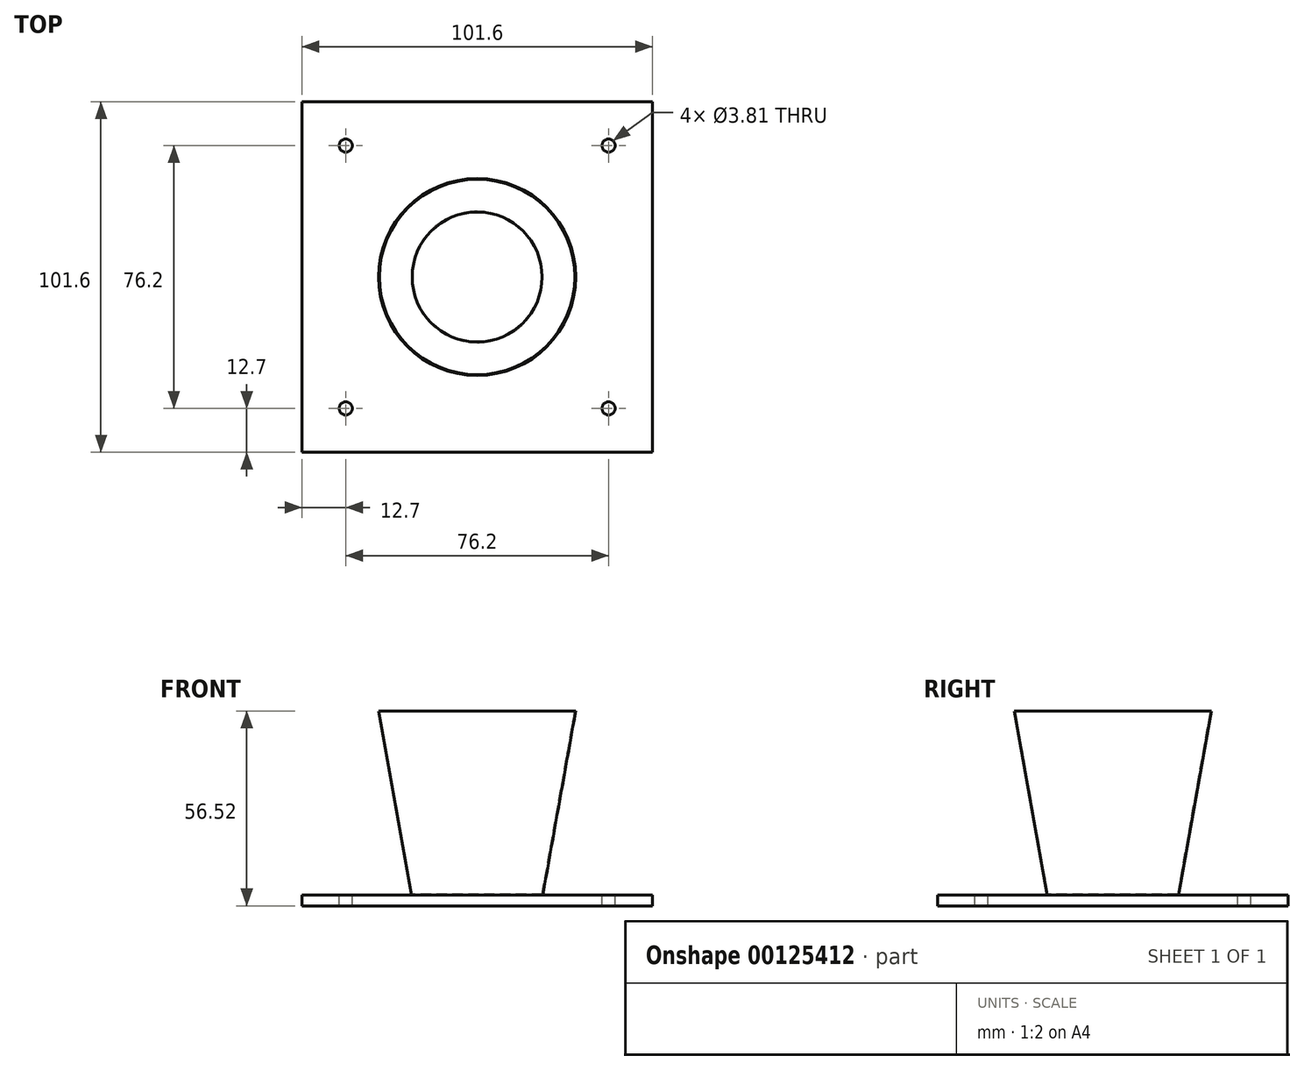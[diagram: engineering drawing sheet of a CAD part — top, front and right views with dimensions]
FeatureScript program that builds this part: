
annotation { "Feature Type Name" : "Feature", "Feature Type Description" : "" }
export const myFeature = defineFeature(function(context is Context, id is Id, definition is map)
    precondition{}
    {
        {
            var Q0;
            Q0=qCreatedBy(makeId("Top.planeOp"),FACE);
            var sketch = newSketch(context, id + "F0", { "sketchPlane" : qUnion([Q0])});
            skCircle(sketch, "E0", {"center": v(0, 0) * mm, "radius": 19.05 * mm});
            skSolve(sketch);
        }
        {
            var Q0;
            Q0=qCreatedBy(makeId("Top.planeOp"),FACE);
            cPlane(context, id + "F1", {"entities" : qUnion([Q0]), "cplaneType" : CPlaneType.OFFSET, "offset" : 53.34 * mm, "width" : 152.4 * mm, "height" : 152.4 * mm});
        }
        {
            var Q0;
            Q0=qCreatedBy(id+"F1.planeOp",FACE);
            var sketch = newSketch(context, id + "F2", { "sketchPlane" : qUnion([Q0])});
            skCircle(sketch, "E1", {"center": v(0, 0) * mm, "radius": 28.58 * mm});
            skSolve(sketch);
        }
        {
            var Q0;
            Q0=makeQuery(id+"F2.imprint","IMPRINT",FACE,{"disambiguationData":[TD([[makeQuery(id+"F2.imprint","IMPRINT",EDGE,{"derivedFrom":sQuery(id+"F2.wireOp",EDGE,"E1")}),1.0]])]});
            var Q1;
            Q1=makeQuery(id+"F0.imprint","IMPRINT",FACE,{"disambiguationData":[TD([[makeQuery(id+"F0.imprint","IMPRINT",EDGE,{"derivedFrom":sQuery(id+"F0.wireOp",EDGE,"E0")}),1.0]])]});
            loft(context, id + "F3", {"sheetProfilesArray" : [{ "sheetProfileEntities" : qUnion([Q0]) }, { "sheetProfileEntities" : qUnion([Q1]) }]});
        }
        {
            var Q0;
            Q0=makeQuery(id+"F3.opLoft","CAP_FACE",FACE,{"disambiguationData":[OSD([makeQuery(id+"F2.imprint","IMPRINT",FACE,{"disambiguationData":[TD([[makeQuery(id+"F2.imprint","IMPRINT",EDGE,{"derivedFrom":sQuery(id+"F2.wireOp",EDGE,"E1")}),1.0]])]})])],"isStart":true});
            shell(context, id + "F4", {"entities" : qUnion([Q0]), "thickness" : 0.25 * mm});
        }
        {
            var Q0;
            Q0=makeQuery(id+"F3.opLoft","CAP_FACE",FACE,{"disambiguationData":[OSD([makeQuery(id+"F0.imprint","IMPRINT",FACE,{"disambiguationData":[TD([[makeQuery(id+"F0.imprint","IMPRINT",EDGE,{"derivedFrom":sQuery(id+"F0.wireOp",EDGE,"E0")}),1.0]])]})])],"isStart":true});
            var sketch = newSketch(context, id + "F5", { "sketchPlane" : qUnion([Q0])});
            skLineSegment(sketch, "E2.bottom", {"start": v(-50.8, 50.8) * mm, "end": v(50.8, 50.8) * mm});
            skLineSegment(sketch, "E2.top", {"start": v(-50.8, -50.8) * mm, "end": v(50.8, -50.8) * mm});
            skLineSegment(sketch, "E2.left", {"start": v(-50.8, 50.8) * mm, "end": v(-50.8, -50.8) * mm});
            skLineSegment(sketch, "E2.right", {"start": v(50.8, 50.8) * mm, "end": v(50.8, -50.8) * mm});
            skCircle(sketch, "E3", {"center": v(-38.1, -38.1) * mm, "radius": 1.9 * mm});
            skCircle(sketch, "E4", {"center": v(-38.1, 38.1) * mm, "radius": 1.9 * mm});
            skCircle(sketch, "E5", {"center": v(38.1, 38.1) * mm, "radius": 1.9 * mm});
            skCircle(sketch, "E6", {"center": v(38.1, -38.1) * mm, "radius": 1.9 * mm});
            skSolve(sketch);
        }
        {
            var Q0;
            Q0=qSketchRegion(id+"F5",true);
            var Q1;
            Q1=makeQuery(id+"F5.imprint","IMPRINT",FACE,{"disambiguationData":[TD([[makeQuery(id+"F5.imprint","IMPRINT",EDGE,{"derivedFrom":sQuery(id+"F5.wireOp",EDGE,"E2.bottom")}),-1.0]])]});
            extrude(context, id + "F6", {"entities" : qUnion([Q0, Q1]), "depth" : 3.17 * mm});
        }
    });
